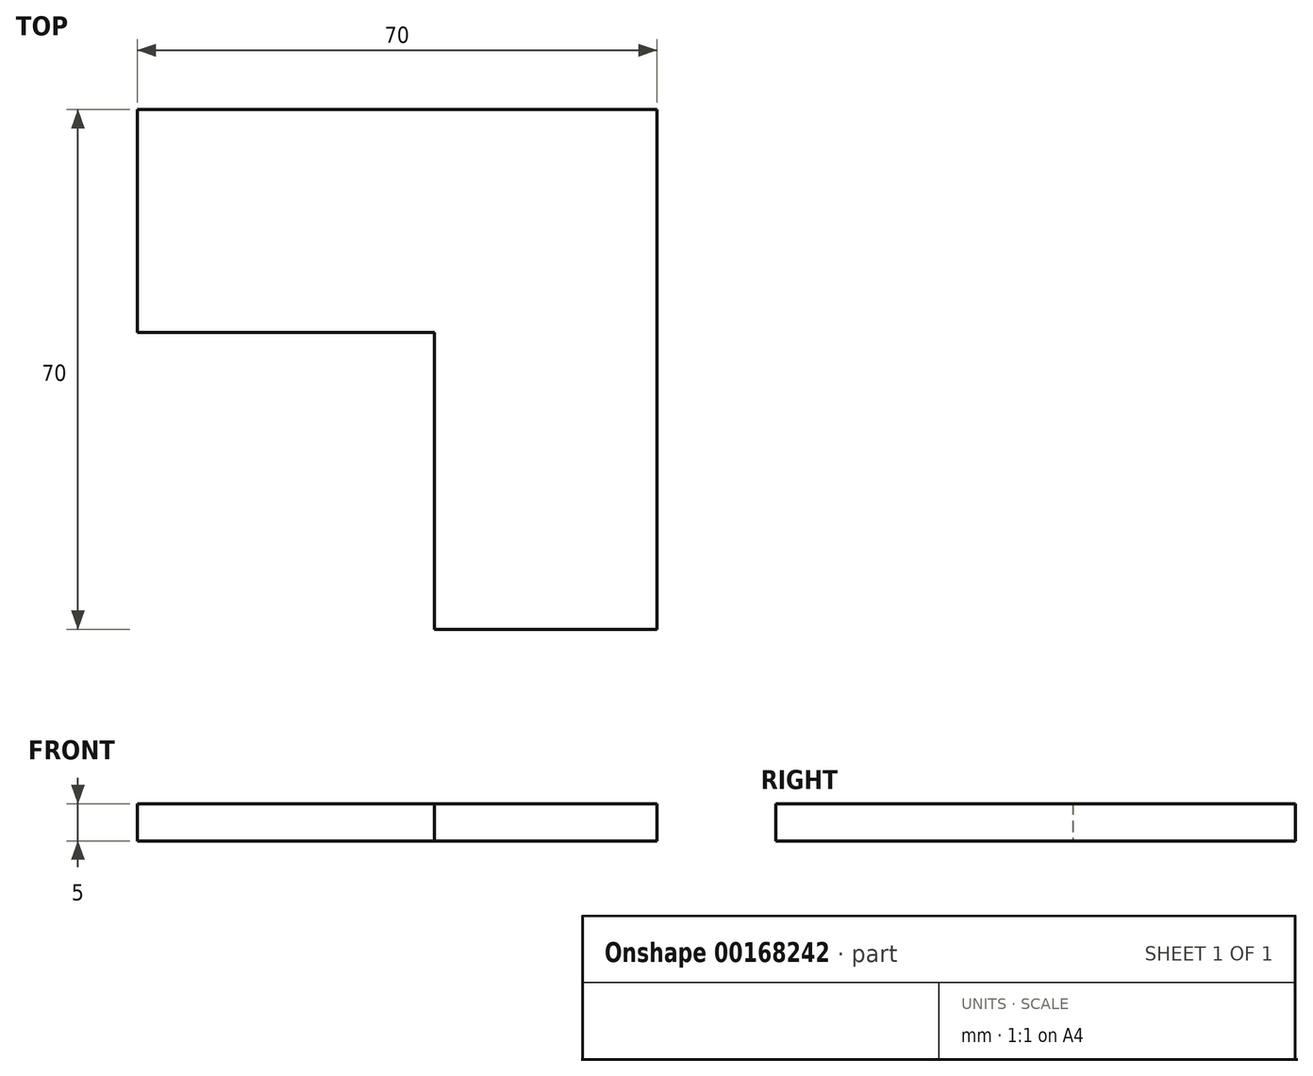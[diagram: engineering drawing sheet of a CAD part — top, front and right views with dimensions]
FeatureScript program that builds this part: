
annotation { "Feature Type Name" : "Feature", "Feature Type Description" : "" }
export const myFeature = defineFeature(function(context is Context, id is Id, definition is map)
    precondition{}
    {
        {
            var Q0;
            Q0=qCreatedBy(makeId("Top.planeOp"),FACE);
            var sketch = newSketch(context, id + "F0", { "sketchPlane" : qUnion([Q0])});
            skLineSegment(sketch, "E0.bottom", {"start": v(35, 35) * mm, "end": v(-35, 35) * mm});
            skLineSegment(sketch, "E0.top", {"start": v(35, -35) * mm, "end": v(5, -35) * mm});
            skLineSegment(sketch, "E0.left", {"start": v(35, 35) * mm, "end": v(35, -35) * mm});
            skLineSegment(sketch, "E0.right", {"start": v(-35, 35) * mm, "end": v(-35, 5) * mm});
            skPoint(sketch, "E0.middle", {"position": v(0, 0) * mm});
            skLineSegment(sketch, "E1", {"start": v(-35, 5) * mm, "end": v(0, 5) * mm});
            skLineSegment(sketch, "E2", {"start": v(5, -35) * mm, "end": v(5, 5) * mm});
            skLineSegment(sketch, "E3", {"start": v(0, 5) * mm, "end": v(5, 5) * mm});
            skPoint(sketch, "E4.orphan", {"position": v(0, -35) * mm});
            skPoint(sketch, "E5.orphan", {"position": v(-35, -35) * mm});
            skSolve(sketch);
        }
        {
            var Q0;
            Q0 = qSketchRegion(id + "F0", true);
            extrude(context, id + "F1", {"entities" : qUnion([Q0]), "depth" : 5 * mm});
        }
    });
